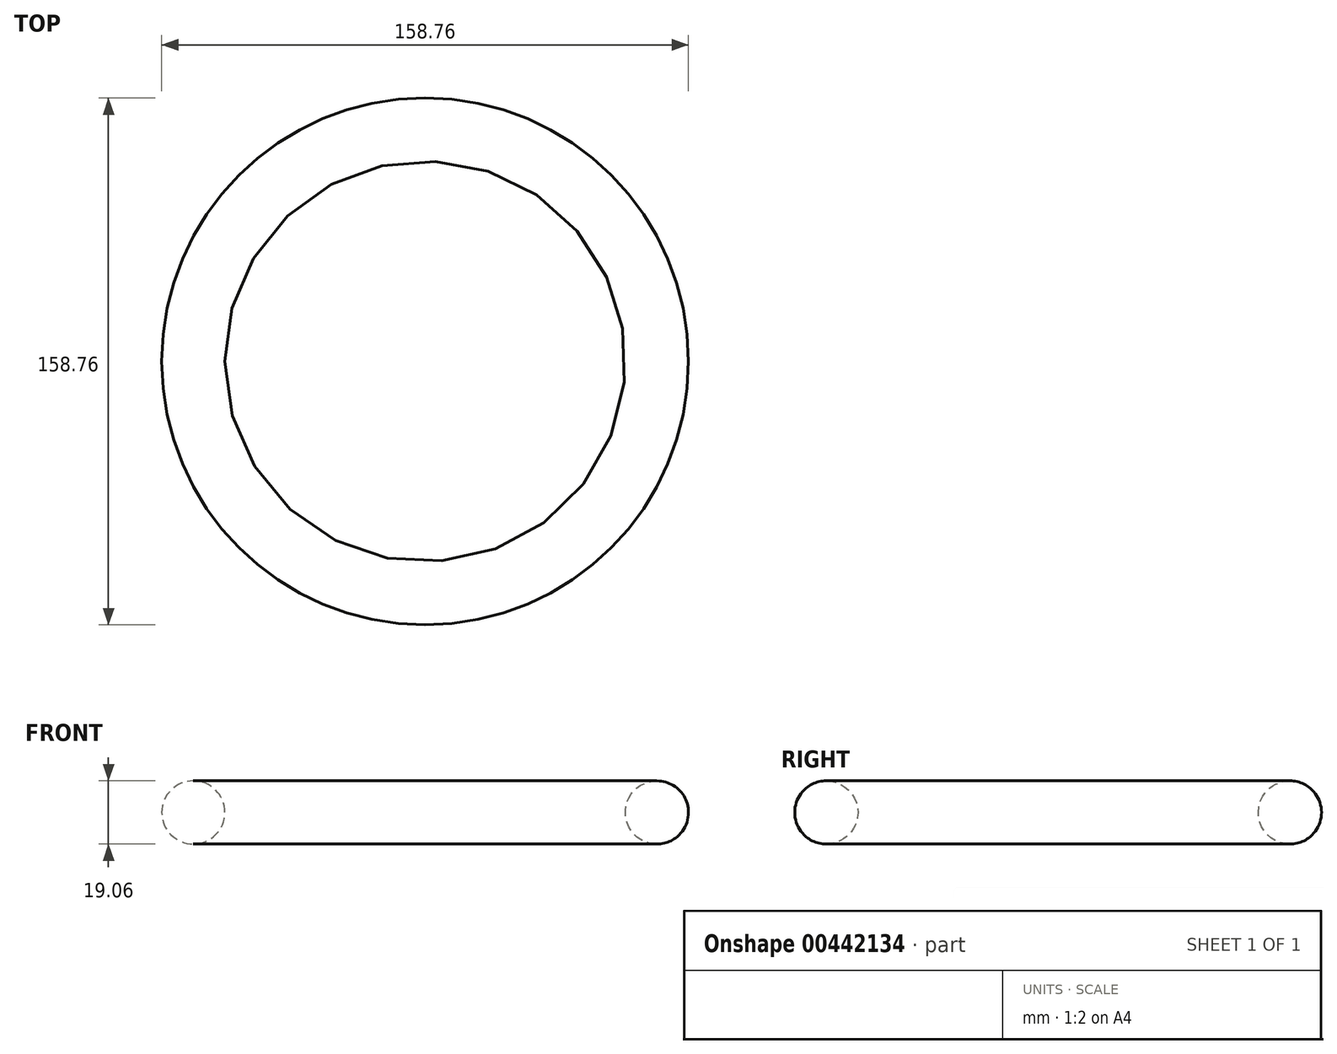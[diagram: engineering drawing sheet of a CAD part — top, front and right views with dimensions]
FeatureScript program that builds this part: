
annotation { "Feature Type Name" : "Feature", "Feature Type Description" : "" }
export const myFeature = defineFeature(function(context is Context, id is Id, definition is map)
    precondition{}
    {
        {
            var Q0;
            Q0=qCreatedBy(makeId("Front.planeOp"),FACE);
            var sketch = newSketch(context, id + "F0", { "sketchPlane" : qUnion([Q0])});
            skCircle(sketch, "E0", {"center": v(69.85, 0) * mm, "radius": 9.53 * mm});
            skLineSegment(sketch, "E1", {"start": v(0, 0) * mm, "end": v(69.85, 0) * mm, "construction": true});
            skLineSegment(sketch, "E2", {"start": v(0, 0) * mm, "end": v(0, 32.6) * mm, "construction": true});
            skSolve(sketch);
        }
        {
            var Q0;
            Q0 = qSketchRegion(id + "F0", true);
            var Q1;
            Q1=sQuery(id+"F0.wireOp",EDGE,"E2");
            revolve(context, id + "F1", {"entities" : qUnion([Q0]), "axis" : qUnion([Q1]), "revolveType" : RevolveType.FULL});
        }
    });
